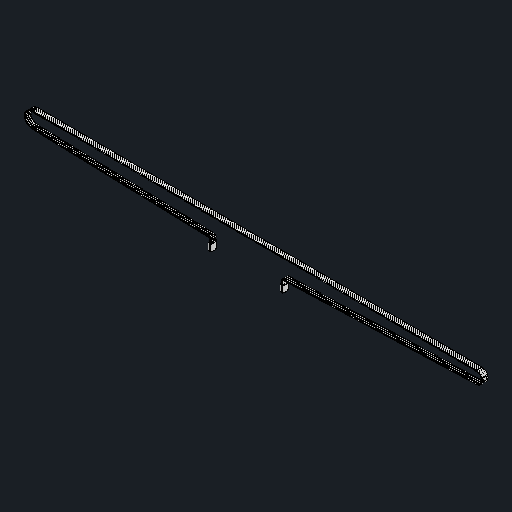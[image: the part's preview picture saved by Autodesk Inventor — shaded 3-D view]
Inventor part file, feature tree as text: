
AUTODESK INVENTOR PART (.ipt)
format: ipt  version: 2024.2 (Build 282272000, 272)  size: 2,002,944 bytes
history: native  units: mm
features: other x4, boolean_combine x1, mirror x1
ambient origin geometry x8: Origin, YZ Plane, XZ Plane, XY Plane, X Axis, Y Axis, Z Axis, Center Point
bodies: Body1 (feature_tree), Body2 (feature_tree), Body3 (feature_tree)
feature tree (6):
  other  "솔리드1"
  other  "솔리드2"
  other  "솔리드3"
  boolean_combine  "Combine1"
  other  "_belt-crimp-ndr_-_Stock-y-axis-belt-ndr-1_"
  mirror  "Mirror1"
